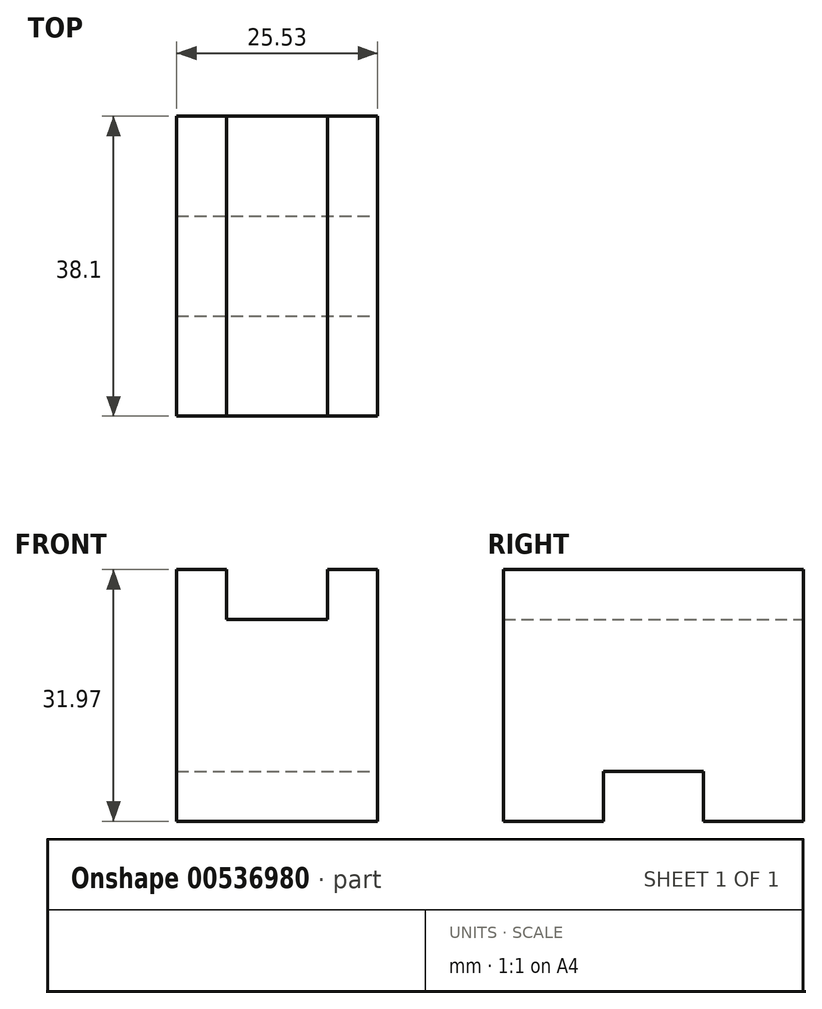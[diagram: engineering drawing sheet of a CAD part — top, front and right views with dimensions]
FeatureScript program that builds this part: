
annotation { "Feature Type Name" : "Feature", "Feature Type Description" : "" }
export const myFeature = defineFeature(function(context is Context, id is Id, definition is map)
    precondition{}
    {
        {
            var Q0;
            Q0=qCreatedBy(makeId("Front.planeOp"),FACE);
            var sketch = newSketch(context, id + "F0", { "sketchPlane" : qUnion([Q0])});
            skLineSegment(sketch, "E0", {"start": v(-58.1, 56.29) * mm, "end": v(-58.1, 24.32) * mm});
            skLineSegment(sketch, "E1", {"start": v(-58.1, 56.29) * mm, "end": v(-32.57, 56.29) * mm});
            skLineSegment(sketch, "E2", {"start": v(-32.57, 56.29) * mm, "end": v(-32.57, 24.32) * mm});
            skLineSegment(sketch, "E3", {"start": v(-32.57, 24.32) * mm, "end": v(-58.1, 24.32) * mm});
            skSolve(sketch);
        }
        {
            var Q0;
            Q0=makeQuery(id+"F0.imprint","IMPRINT",FACE,{"disambiguationData":[TD([[makeQuery(id+"F0.imprint","IMPRINT",EDGE,{"derivedFrom":sQuery(id+"F0.wireOp",EDGE,"E0")}),1.0]])]});
            extrude(context, id + "F1", {"entities" : qUnion([Q0]), "depth" : 25.4 * mm, "offsetDistance" : 25.4 * mm});
        }
        {
            var Q0;
            Q0=makeQuery(id+"F1.opExtrude","CAP_FACE",FACE,{"disambiguationData":[OSD([sQuery(id+"F0.wireOp",EDGE,"E0"),sQuery(id+"F0.wireOp",EDGE,"E1"),sQuery(id+"F0.wireOp",EDGE,"E2"),sQuery(id+"F0.wireOp",EDGE,"E3")])],"isStart":true});
            var sketch = newSketch(context, id + "F2", { "sketchPlane" : qUnion([Q0])});
            skLineSegment(sketch, "E4", {"start": v(38.92, 56.29) * mm, "end": v(38.92, 49.94) * mm});
            skLineSegment(sketch, "E5", {"start": v(38.92, 49.94) * mm, "end": v(51.75, 49.94) * mm});
            skLineSegment(sketch, "E6", {"start": v(51.75, 49.94) * mm, "end": v(51.75, 56.29) * mm});
            skSolve(sketch);
        }
        {
            var Q0;
            {var subQ0=sQuery(id+"F2.wireOp",EDGE,"E4");Q0=makeQuery(id+"F2.imprint","IMPRINT",FACE,{"disambiguationData":[TD([[makeQuery(id+"F2.imprint","IMPRINT",EDGE,{"derivedFrom":subQ0}),1.0]])]});}
            extrude(context, id + "F3", {"entities" : qUnion([Q0]), "operationType" : NewBodyOperationType.REMOVE, "endBound" : BoundingType.THROUGH_ALL, "oppositeDirection" : true, "depth" : 25.4 * mm, "offsetDistance" : 25.4 * mm});
        }
        {
            var Q0;
            Q0=makeQuery(id+"F1.opExtrude","CAP_FACE",FACE,{"disambiguationData":[OSD([sQuery(id+"F0.wireOp",EDGE,"E0"),sQuery(id+"F0.wireOp",EDGE,"E1"),sQuery(id+"F0.wireOp",EDGE,"E2"),sQuery(id+"F0.wireOp",EDGE,"E3")])],"isStart":false});
            extrude(context, id + "F4", {"entities" : qUnion([Q0]), "operationType" : NewBodyOperationType.ADD, "depth" : 12.7 * mm, "offsetDistance" : 25.4 * mm});
        }
        {
            var Q0;
            {var subQ0=sQuery(id+"F0.wireOp",EDGE,"E2");Q0=makeQuery(id+"F4.boolean.opBoolean","MERGE",FACE,{"derivedFrom":[makeQuery(id+"F1.opExtrude","SWEPT_FACE",FACE,{"disambiguationData":[OSD([subQ0])]}),makeQuery(id+"F4.opExtrude","SWEPT_FACE",FACE,{"disambiguationData":[OSD([subQ0])]})]});}
            var sketch = newSketch(context, id + "F5", { "sketchPlane" : qUnion([Q0])});
            skLineSegment(sketch, "E7", {"start": v(-25.4, 24.32) * mm, "end": v(-25.4, 30.67) * mm});
            skLineSegment(sketch, "E8", {"start": v(-25.4, 30.67) * mm, "end": v(-12.7, 30.67) * mm});
            skLineSegment(sketch, "E9", {"start": v(-12.7, 30.67) * mm, "end": v(-12.7, 24.32) * mm});
            skSolve(sketch);
        }
        {
            var Q0;
            Q0 = qSketchRegion(id + "F5", true);
            var Q1;
            {var subQ0=sQuery(id+"F5.wireOp",EDGE,"E7");Q1=makeQuery(id+"F5.imprint","IMPRINT",FACE,{"disambiguationData":[TD([[makeQuery(id+"F5.imprint","IMPRINT",EDGE,{"derivedFrom":subQ0}),-1.0]])]});}
            extrude(context, id + "F6", {"entities" : qUnion([Q0, Q1]), "operationType" : NewBodyOperationType.REMOVE, "endBound" : BoundingType.THROUGH_ALL, "oppositeDirection" : true, "depth" : 25.4 * mm, "offsetDistance" : 25.4 * mm});
        }
    });
